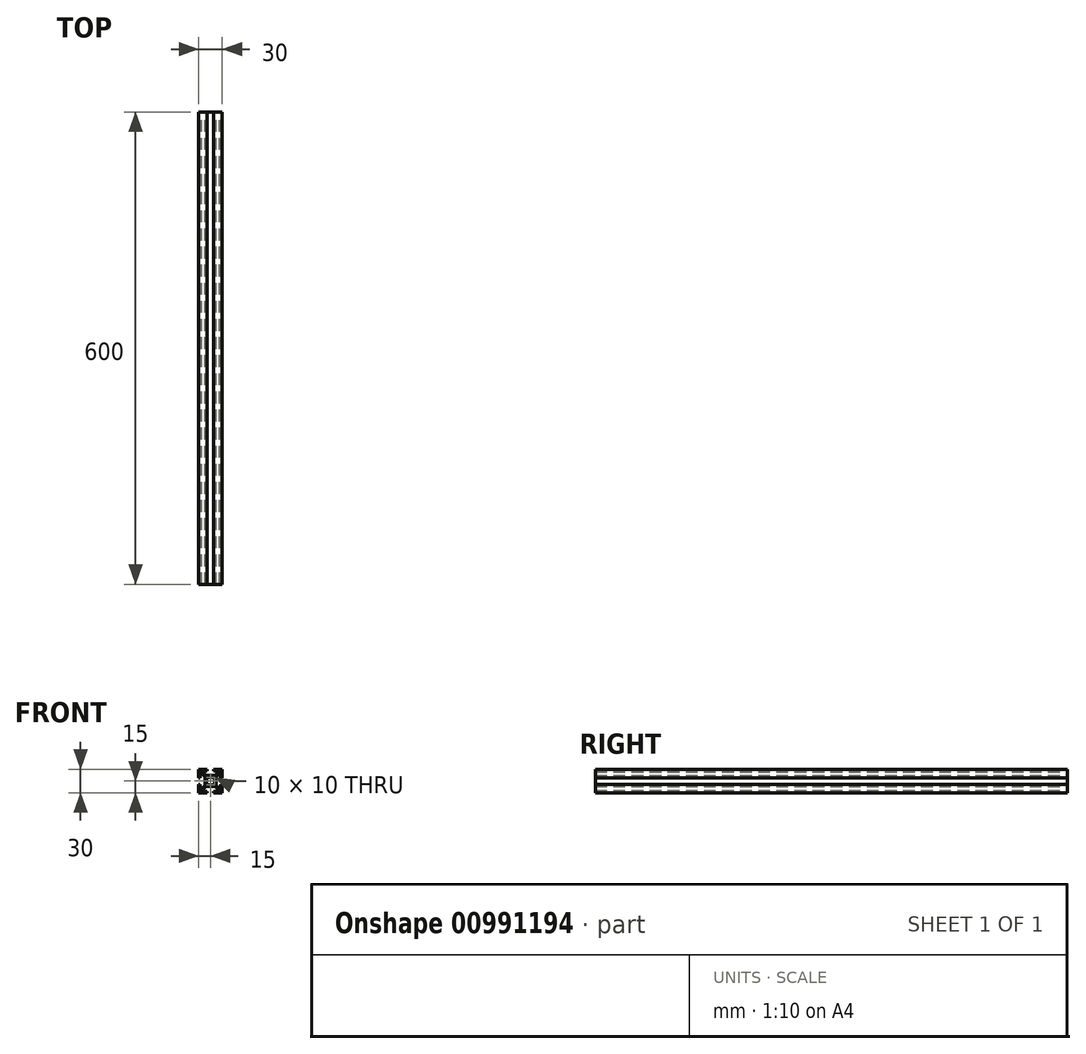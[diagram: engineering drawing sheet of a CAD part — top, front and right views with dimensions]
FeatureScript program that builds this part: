
annotation { "Feature Type Name" : "Feature", "Feature Type Description" : "" }
export const myFeature = defineFeature(function(context is Context, id is Id, definition is map)
    precondition{}
    {
        {
            assignVariable(context, id + "F0", {"variableType" : VariableType.LENGTH, "name" : "length", "lengthValue" : 600 * mm});
        }
        {
            var Q0;
            Q0=qCreatedBy(makeId("Front.planeOp"),FACE);
            var sketch = newSketch(context, id + "F1", { "sketchPlane" : qUnion([Q0])});
            skLineSegment(sketch, "E0.bottom", {"start": v(5, -5) * mm, "end": v(-5, -5) * mm});
            skLineSegment(sketch, "E0.top", {"start": v(5, 5) * mm, "end": v(-5, 5) * mm});
            skLineSegment(sketch, "E0.left", {"start": v(5, -5) * mm, "end": v(5, 5) * mm});
            skLineSegment(sketch, "E0.right", {"start": v(-5, -5) * mm, "end": v(-5, 5) * mm});
            skPoint(sketch, "E0.middle", {"position": v(0, 0) * mm});
            skLineSegment(sketch, "E1.bottom", {"start": v(7, -7) * mm, "end": v(-7, -7) * mm});
            skLineSegment(sketch, "E1.top", {"start": v(7, 7) * mm, "end": v(-7, 7) * mm});
            skLineSegment(sketch, "E1.left", {"start": v(7, -7) * mm, "end": v(7, 7) * mm});
            skLineSegment(sketch, "E1.right", {"start": v(-7, -7) * mm, "end": v(-7, 7) * mm});
            skLineSegment(sketch, "E2", {"start": v(0, 0) * mm, "end": v(-25.51, 25.51) * mm, "construction": true});
            skLineSegment(sketch, "E3", {"start": v(0, 0) * mm, "end": v(19.59, 19.59) * mm, "construction": true});
            skLineSegment(sketch, "E4", {"start": v(-15, 15) * mm, "end": v(15, 15) * mm, "construction": true});
            skLineSegment(sketch, "E5", {"start": v(-15, 15) * mm, "end": v(-4, 15) * mm});
            skLineSegment(sketch, "E6", {"start": v(-4, 15) * mm, "end": v(-4, 13) * mm});
            skLineSegment(sketch, "E7", {"start": v(-4, 13) * mm, "end": v(-13, 13) * mm});
            skLineSegment(sketch, "E8", {"start": v(15, 15) * mm, "end": v(4, 15) * mm});
            skLineSegment(sketch, "E9", {"start": v(4, 15) * mm, "end": v(4, 13) * mm});
            skLineSegment(sketch, "E10", {"start": v(4, 13) * mm, "end": v(13, 13) * mm});
            skLineSegment(sketch, "E11", {"start": v(-15, 15) * mm, "end": v(-15, 4) * mm});
            skLineSegment(sketch, "E12", {"start": v(-15, 4) * mm, "end": v(-13, 4) * mm});
            skLineSegment(sketch, "E13", {"start": v(-13, 4) * mm, "end": v(-13, 13) * mm});
            skLineSegment(sketch, "E14", {"start": v(13, 13) * mm, "end": v(13, 4) * mm});
            skLineSegment(sketch, "E15", {"start": v(13, 4) * mm, "end": v(15, 4) * mm});
            skLineSegment(sketch, "E16", {"start": v(15, 4) * mm, "end": v(15, 15) * mm});
            skLineSegment(sketch, "E17", {"start": v(-11.59, 13) * mm, "end": v(-5.59, 7) * mm});
            skLineSegment(sketch, "E18", {"start": v(-13, 11.65) * mm, "end": v(-7, 5.65) * mm});
            skLineSegment(sketch, "E19", {"start": v(0, 0) * mm, "end": v(18.62, -18.62) * mm, "construction": true});
            skLineSegment(sketch, "E20", {"start": v(0, 0) * mm, "end": v(-17.26, -17.26) * mm, "construction": true});
            skLineSegment(sketch, "E21", {"start": v(-15, -15) * mm, "end": v(-15, -4) * mm});
            skLineSegment(sketch, "E22", {"start": v(-15, -4) * mm, "end": v(-13, -4) * mm});
            skLineSegment(sketch, "E23", {"start": v(-13, -4) * mm, "end": v(-13, -13) * mm});
            skLineSegment(sketch, "E24", {"start": v(13, -13) * mm, "end": v(13, -4) * mm});
            skLineSegment(sketch, "E25", {"start": v(13, -4) * mm, "end": v(15, -4) * mm});
            skLineSegment(sketch, "E26", {"start": v(15, -4) * mm, "end": v(15, -15) * mm});
            skLineSegment(sketch, "E27", {"start": v(5.59, 7) * mm, "end": v(11.59, 13) * mm});
            skLineSegment(sketch, "E28", {"start": v(7, 5.59) * mm, "end": v(13, 11.59) * mm});
            skLineSegment(sketch, "E29", {"start": v(-13, -11.59) * mm, "end": v(-7, -5.59) * mm});
            skLineSegment(sketch, "E30", {"start": v(-11.59, -13) * mm, "end": v(-5.59, -7) * mm});
            skLineSegment(sketch, "E31", {"start": v(-4, -13) * mm, "end": v(-4, -15) * mm});
            skLineSegment(sketch, "E32", {"start": v(4, -13) * mm, "end": v(4, -15) * mm});
            skLineSegment(sketch, "E33", {"start": v(-13, -13) * mm, "end": v(-11.59, -13) * mm});
            skLineSegment(sketch, "E34", {"start": v(-4, -13) * mm, "end": v(-11.59, -13) * mm});
            skLineSegment(sketch, "E35", {"start": v(-4, -15) * mm, "end": v(-15, -15) * mm});
            skLineSegment(sketch, "E36", {"start": v(4, -13) * mm, "end": v(13, -13) * mm});
            skLineSegment(sketch, "E37", {"start": v(4, -15) * mm, "end": v(15, -15) * mm});
            skLineSegment(sketch, "E38", {"start": v(7, -5.59) * mm, "end": v(13, -11.59) * mm});
            skLineSegment(sketch, "E39", {"start": v(5.59, -7) * mm, "end": v(11.59, -13) * mm});
            skSolve(sketch);
        }
        {
            var Q0;
            Q0=makeQuery(id+"F1.imprint","IMPRINT",FACE,{"disambiguationData":[TD([[makeQuery(id+"F1.imprint","IMPRINT",EDGE,{"derivedFrom":sQuery(id+"F1.wireOp",EDGE,"E5")}),-1.0]])]});
            var Q1;
            {var subQ7=sQuery(id+"F1.wireOp",EDGE,"E17");Q1=makeQuery(id+"F1.imprint","IMPRINT",FACE,{"disambiguationData":[TD([[makeQuery(id+"F1.imprint","IMPRINT",EDGE,{"derivedFrom":subQ7}),-1.0]])]});}
            var Q2;
            Q2=makeQuery(id+"F1.imprint","IMPRINT",FACE,{"disambiguationData":[TD([[makeQuery(id+"F1.imprint","IMPRINT",EDGE,{"derivedFrom":sQuery(id+"F1.wireOp",EDGE,"E8")}),1.0]])]});
            var Q3;
            {var subQ4=sQuery(id+"F1.wireOp",EDGE,"E27");Q3=makeQuery(id+"F1.imprint","IMPRINT",FACE,{"disambiguationData":[TD([[makeQuery(id+"F1.imprint","IMPRINT",EDGE,{"derivedFrom":subQ4}),-1.0]])]});}
            var Q4;
            Q4=makeQuery(id+"F1.imprint","IMPRINT",FACE,{"disambiguationData":[TD([[makeQuery(id+"F1.imprint","IMPRINT",EDGE,{"derivedFrom":sQuery(id+"F1.wireOp",EDGE,"E0.bottom")}),1.0]])]});
            var Q5;
            {var subQ4=sQuery(id+"F1.wireOp",EDGE,"E25");Q5=makeQuery(id+"F1.imprint","IMPRINT",FACE,{"disambiguationData":[TD([[makeQuery(id+"F1.imprint","IMPRINT",EDGE,{"derivedFrom":subQ4}),-1.0]])]});}
            var Q6;
            {var subQ4=sQuery(id+"F1.wireOp",EDGE,"E38");Q6=makeQuery(id+"F1.imprint","IMPRINT",FACE,{"disambiguationData":[TD([[makeQuery(id+"F1.imprint","IMPRINT",EDGE,{"derivedFrom":subQ4}),-1.0]])]});}
            var Q7;
            Q7=makeQuery(id+"F1.imprint","IMPRINT",FACE,{"disambiguationData":[TD([[makeQuery(id+"F1.imprint","IMPRINT",EDGE,{"derivedFrom":sQuery(id+"F1.wireOp",EDGE,"E21")}),-1.0]])]});
            var Q8;
            {var subQ0=sQuery(id+"F1.wireOp",EDGE,"E29");Q8=makeQuery(id+"F1.imprint","IMPRINT",FACE,{"disambiguationData":[TD([[makeQuery(id+"F1.imprint","IMPRINT",EDGE,{"derivedFrom":subQ0}),-1.0]])]});}
            extrude(context, id + "F2", {"entities" : qUnion([Q0, Q1, Q2, Q3, Q4, Q5, Q6, Q7, Q8]), "depth" : getVariable(context, 'length'), "offsetDistance" : 25 * mm});
        }
    });
